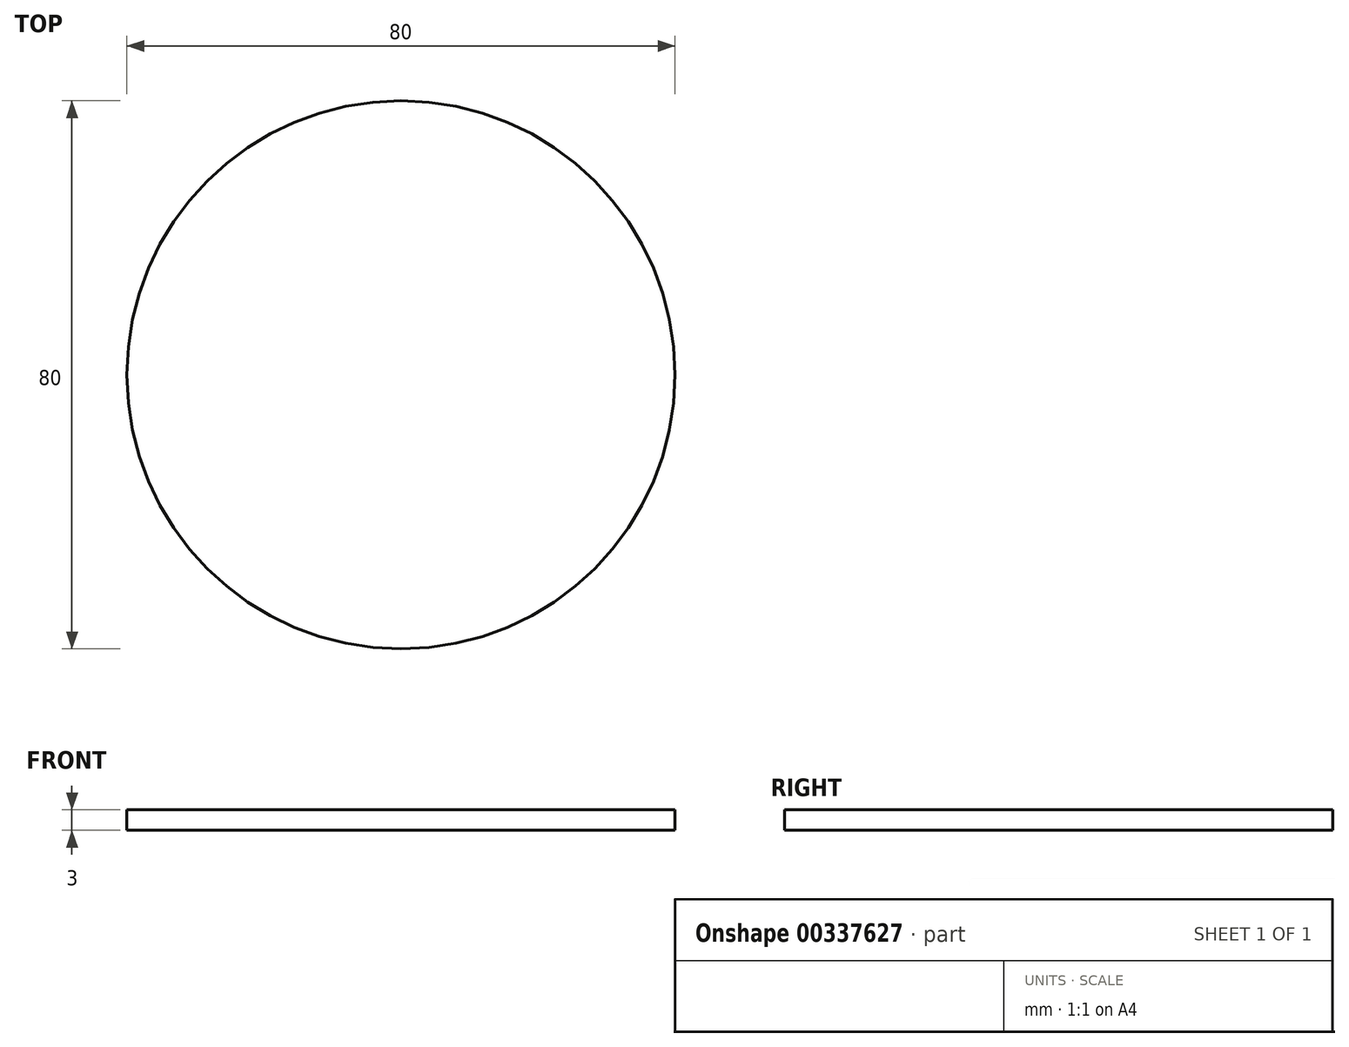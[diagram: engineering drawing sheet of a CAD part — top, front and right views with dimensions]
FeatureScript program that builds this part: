
annotation { "Feature Type Name" : "Feature", "Feature Type Description" : "" }
export const myFeature = defineFeature(function(context is Context, id is Id, definition is map)
    precondition{}
    {
        {
            var Q0;
            Q0=qCreatedBy(makeId("Top.planeOp"),FACE);
            var sketch = newSketch(context, id + "F0", { "sketchPlane" : qUnion([Q0])});
            skCircle(sketch, "E0", {"center": v(0, 0) * mm, "radius": 40 * mm});
            skSolve(sketch);
        }
        {
            var Q0;
            Q0=makeQuery(id+"F0.imprint","IMPRINT",FACE,{"disambiguationData":[TD([[makeQuery(id+"F0.imprint","IMPRINT",EDGE,{"derivedFrom":sQuery(id+"F0.wireOp",EDGE,"E0")}),1.0]])]});
            extrude(context, id + "F1", {"entities" : qUnion([Q0]), "depth" : 3 * mm});
        }
    });
